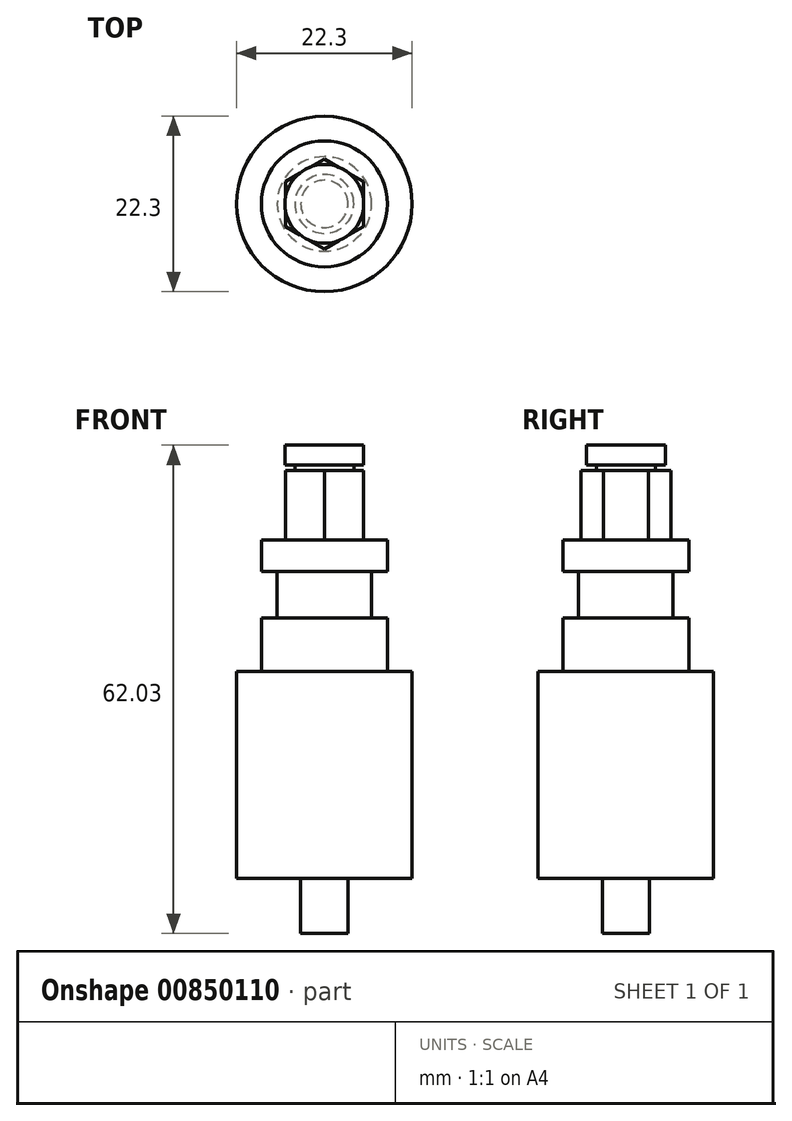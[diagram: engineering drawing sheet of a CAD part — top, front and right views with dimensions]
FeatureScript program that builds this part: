
annotation { "Feature Type Name" : "Feature", "Feature Type Description" : "" }
export const myFeature = defineFeature(function(context is Context, id is Id, definition is map)
    precondition{}
    {
        {
            var Q0;
            Q0=qCreatedBy(makeId("Top.planeOp"),FACE);
            var sketch = newSketch(context, id + "F0", { "sketchPlane" : qUnion([Q0])});
            skCircle(sketch, "E0", {"center": v(0, 0) * mm, "radius": 3 * mm});
            skSolve(sketch);
        }
        {
            var Q0;
            Q0 = qSketchRegion(id + "F0", true);
            extrude(context, id + "F1", {"entities" : qUnion([Q0]), "depth" : 7 * mm, "offsetDistance" : 25 * mm});
        }
        {
            var Q0;
            Q0=makeQuery(id+"F1.opExtrude","CAP_FACE",FACE,{"disambiguationData":[OSD([sQuery(id+"F0.wireOp",EDGE,"E0")])],"isStart":false});
            var sketch = newSketch(context, id + "F2", { "sketchPlane" : qUnion([Q0])});
            skCircle(sketch, "E1", {"center": v(0, 0) * mm, "radius": 11.15 * mm});
            skSolve(sketch);
        }
        {
            var Q0;
            Q0 = qSketchRegion(id + "F2", true);
            extrude(context, id + "F3", {"entities" : qUnion([Q0]), "operationType" : NewBodyOperationType.ADD, "depth" : 26.25 * mm, "offsetDistance" : 25 * mm});
        }
        {
            var Q0;
            Q0=makeQuery(id+"F3.opExtrude","CAP_FACE",FACE,{"disambiguationData":[OSD([sQuery(id+"F2.wireOp",EDGE,"E1")])],"isStart":false});
            var sketch = newSketch(context, id + "F4", { "sketchPlane" : qUnion([Q0])});
            skCircle(sketch, "E2", {"center": v(0, 0) * mm, "radius": 8 * mm});
            skSolve(sketch);
        }
        {
            var Q0;
            Q0 = qSketchRegion(id + "F4", true);
            extrude(context, id + "F5", {"entities" : qUnion([Q0]), "operationType" : NewBodyOperationType.ADD, "depth" : 6.85 * mm, "offsetDistance" : 25 * mm});
        }
        {
            var Q0;
            Q0=makeQuery(id+"F5.opExtrude","CAP_FACE",FACE,{"disambiguationData":[OSD([sQuery(id+"F4.wireOp",EDGE,"E2")])],"isStart":false});
            var sketch = newSketch(context, id + "F6", { "sketchPlane" : qUnion([Q0])});
            skCircle(sketch, "E3", {"center": v(0, 0) * mm, "radius": 6 * mm});
            skSolve(sketch);
        }
        {
            var Q0;
            Q0 = qSketchRegion(id + "F6", true);
            extrude(context, id + "F7", {"entities" : qUnion([Q0]), "operationType" : NewBodyOperationType.ADD, "depth" : 5.88 * mm, "offsetDistance" : 25 * mm});
        }
        {
            var Q0;
            Q0=makeQuery(id+"F7.opExtrude","CAP_FACE",FACE,{"disambiguationData":[OSD([sQuery(id+"F6.wireOp",EDGE,"E3")])],"isStart":false});
            var sketch = newSketch(context, id + "F8", { "sketchPlane" : qUnion([Q0])});
            skCircle(sketch, "E4", {"center": v(0, 0) * mm, "radius": 8 * mm});
            skSolve(sketch);
        }
        {
            var Q0;
            Q0 = qSketchRegion(id + "F8", true);
            extrude(context, id + "F9", {"entities" : qUnion([Q0]), "operationType" : NewBodyOperationType.ADD, "depth" : 4 * mm, "offsetDistance" : 25 * mm});
        }
        {
            var Q0;
            Q0=makeQuery(id+"F9.opExtrude","CAP_FACE",FACE,{"disambiguationData":[OSD([sQuery(id+"F8.wireOp",EDGE,"E4")])],"isStart":false});
            var sketch = newSketch(context, id + "F10", { "sketchPlane" : qUnion([Q0])});
            skCircle(sketch, "E5.cCircle", {"center": v(0, 0) * mm, "radius": 4.95 * mm, "construction": true});
            skLineSegment(sketch, "E5.0", {"start": v(-4.95, -2.86) * mm, "end": v(-4.95, 2.86) * mm});
            skLineSegment(sketch, "E5.1", {"start": v(-4.95, 2.86) * mm, "end": v(0, 5.72) * mm});
            skLineSegment(sketch, "E5.2", {"start": v(0, 5.72) * mm, "end": v(4.95, 2.86) * mm});
            skLineSegment(sketch, "E5.3", {"start": v(4.95, 2.86) * mm, "end": v(4.95, -2.86) * mm});
            skLineSegment(sketch, "E5.4", {"start": v(4.95, -2.86) * mm, "end": v(0, -5.72) * mm});
            skLineSegment(sketch, "E5.5", {"start": v(0, -5.72) * mm, "end": v(-4.95, -2.86) * mm});
            skPoint(sketch, "E5.0.midPoint", {"position": v(-4.95, 0) * mm});
            skSolve(sketch);
        }
        {
            var Q0;
            Q0 = qSketchRegion(id + "F10", true);
            extrude(context, id + "F11", {"entities" : qUnion([Q0]), "operationType" : NewBodyOperationType.ADD, "depth" : 8.8 * mm, "offsetDistance" : 25 * mm});
        }
        {
            var Q0;
            Q0=makeQuery(id+"F11.opExtrude","CAP_FACE",FACE,{"disambiguationData":[OSD([sQuery(id+"F10.wireOp",EDGE,"E5.0"),sQuery(id+"F10.wireOp",EDGE,"E5.1"),sQuery(id+"F10.wireOp",EDGE,"E5.2"),sQuery(id+"F10.wireOp",EDGE,"E5.3"),sQuery(id+"F10.wireOp",EDGE,"E5.4"),sQuery(id+"F10.wireOp",EDGE,"E5.5")])],"isStart":false});
            var sketch = newSketch(context, id + "F12", { "sketchPlane" : qUnion([Q0])});
            skCircle(sketch, "E6", {"center": v(0, 0) * mm, "radius": 3.75 * mm});
            skSolve(sketch);
        }
        {
            var Q0;
            Q0 = qSketchRegion(id + "F12", true);
            extrude(context, id + "F13", {"entities" : qUnion([Q0]), "operationType" : NewBodyOperationType.ADD, "depth" : 0.75 * mm, "offsetDistance" : 25 * mm});
        }
        {
            var Q0;
            Q0=makeQuery(id+"F13.opExtrude","CAP_FACE",FACE,{"disambiguationData":[OSD([sQuery(id+"F12.wireOp",EDGE,"E6")])],"isStart":false});
            var sketch = newSketch(context, id + "F14", { "sketchPlane" : qUnion([Q0])});
            skCircle(sketch, "E7", {"center": v(0, 0) * mm, "radius": 5 * mm});
            skSolve(sketch);
        }
        {
            var Q0;
            Q0 = qSketchRegion(id + "F14", true);
            extrude(context, id + "F15", {"entities" : qUnion([Q0]), "operationType" : NewBodyOperationType.ADD, "depth" : 2.5 * mm, "offsetDistance" : 25 * mm});
        }
    });
